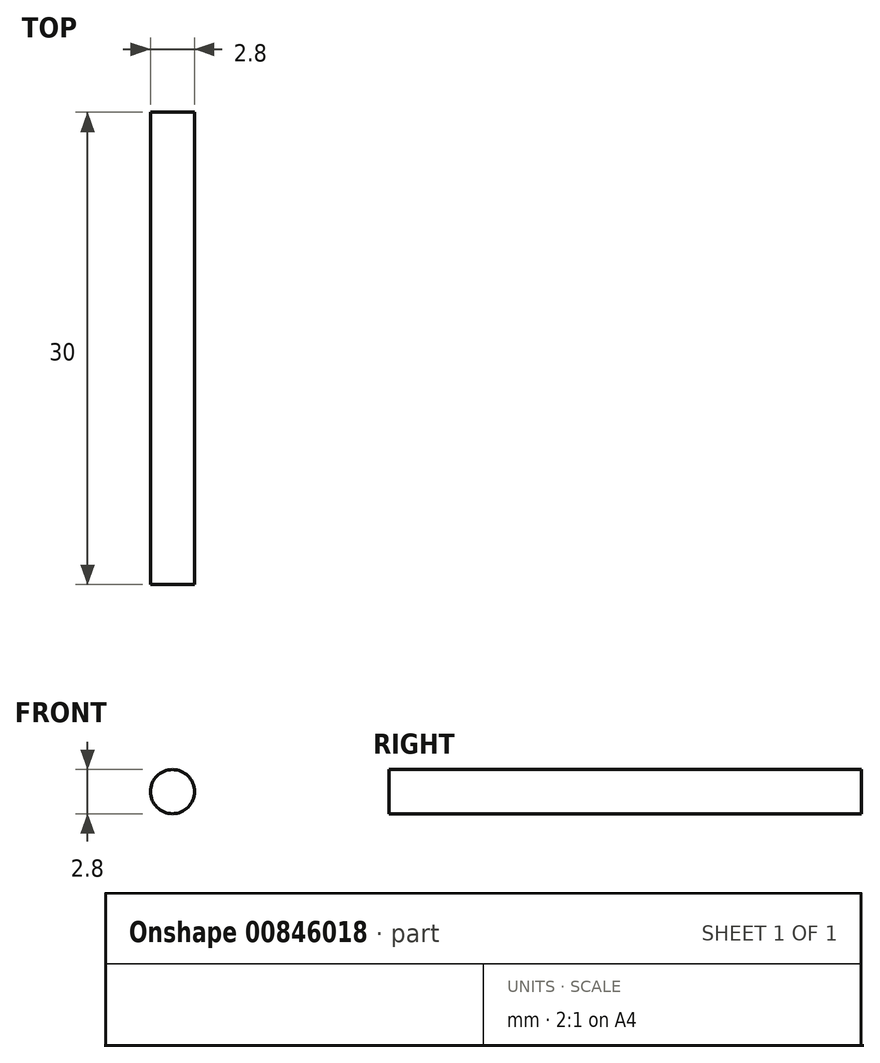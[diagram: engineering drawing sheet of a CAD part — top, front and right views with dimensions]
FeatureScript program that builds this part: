
annotation { "Feature Type Name" : "Feature", "Feature Type Description" : "" }
export const myFeature = defineFeature(function(context is Context, id is Id, definition is map)
    precondition{}
    {
        {
            var Q0;
            Q0=qCreatedBy(makeId("Front.planeOp"),FACE);
            var sketch = newSketch(context, id + "F0", { "sketchPlane" : qUnion([Q0])});
            skCircle(sketch, "E0", {"center": v(0, 1.4) * mm, "radius": 1.4 * mm});
            skSolve(sketch);
        }
        {
            var Q0;
            Q0=makeQuery(id+"F0.imprint","IMPRINT",FACE,{"disambiguationData":[TD([[makeQuery(id+"F0.imprint","IMPRINT",EDGE,{"derivedFrom":sQuery(id+"F0.wireOp",EDGE,"E0")}),1.0]])]});
            extrude(context, id + "F1", {"entities" : qUnion([Q0]), "oppositeDirection" : true, "depth" : 15 * mm, "offsetDistance" : 25 * mm, "hasSecondDirection" : true, "secondDirectionOppositeDirection" : false, "secondDirectionDepth" : 15 * mm});
        }
    });
